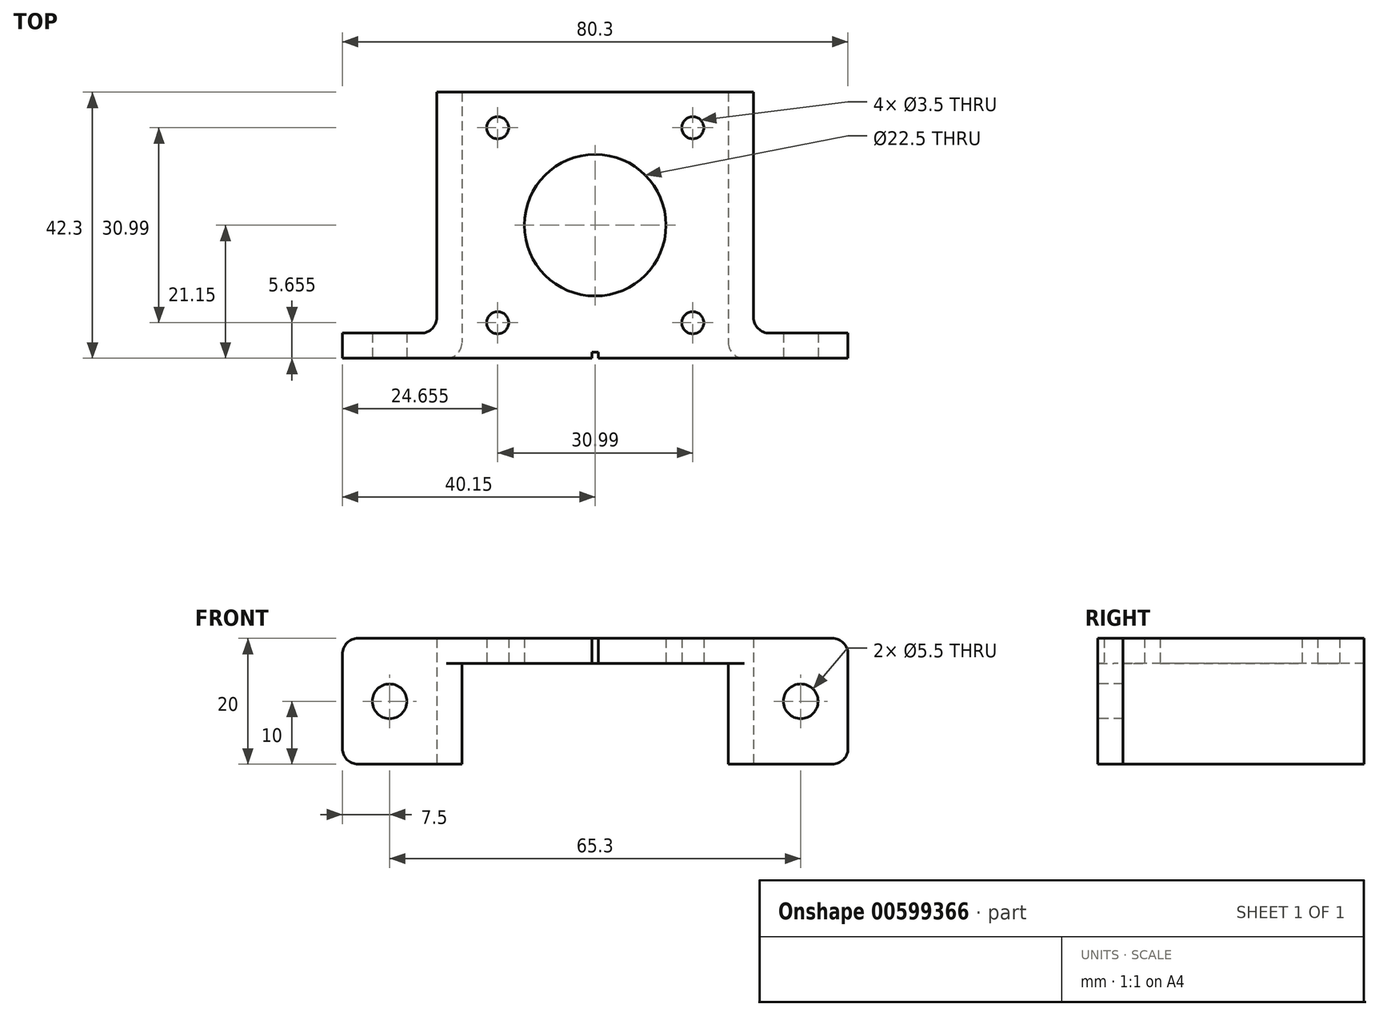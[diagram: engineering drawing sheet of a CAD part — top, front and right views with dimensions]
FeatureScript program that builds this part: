
annotation { "Feature Type Name" : "Feature", "Feature Type Description" : "" }
export const myFeature = defineFeature(function(context is Context, id is Id, definition is map)
    precondition{}
    {
        {
            var Q0;
            Q0=qCreatedBy(makeId("Top.planeOp"),FACE);
            var sketch = newSketch(context, id + "F0", { "sketchPlane" : qUnion([Q0])});
            skLineSegment(sketch, "E0.bottom", {"start": v(-21.15, 21.15) * mm, "end": v(21.15, 21.15) * mm});
            skLineSegment(sketch, "E0.left", {"start": v(-21.15, 21.15) * mm, "end": v(-21.15, -21.15) * mm, "construction": true});
            skLineSegment(sketch, "E0.right", {"start": v(21.15, 21.15) * mm, "end": v(21.15, -21.15) * mm, "construction": true});
            skLineSegment(sketch, "E1.bottom", {"start": v(-15.5, 15.5) * mm, "end": v(15.5, 15.5) * mm, "construction": true});
            skLineSegment(sketch, "E1.top", {"start": v(-15.5, -15.5) * mm, "end": v(15.5, -15.5) * mm, "construction": true});
            skLineSegment(sketch, "E1.left", {"start": v(-15.5, 15.5) * mm, "end": v(-15.5, -15.5) * mm, "construction": true});
            skLineSegment(sketch, "E1.right", {"start": v(15.5, 15.5) * mm, "end": v(15.5, -15.5) * mm, "construction": true});
            skCircle(sketch, "E2", {"center": v(-15.5, 15.5) * mm, "radius": 1.75 * mm});
            skCircle(sketch, "E3", {"center": v(-15.5, -15.5) * mm, "radius": 1.75 * mm});
            skCircle(sketch, "E4", {"center": v(15.5, 15.5) * mm, "radius": 1.75 * mm});
            skCircle(sketch, "E5", {"center": v(15.5, -15.5) * mm, "radius": 1.75 * mm});
            skCircle(sketch, "E6", {"center": v(0, 0) * mm, "radius": 11.25 * mm});
            skLineSegment(sketch, "E7", {"start": v(-21.15, -21.15) * mm, "end": v(21.15, -21.15) * mm});
            skLineSegment(sketch, "E8.bottom", {"start": v(21.15, -21.15) * mm, "end": v(40.15, -21.15) * mm});
            skLineSegment(sketch, "E8.top", {"start": v(21.15, -17.15) * mm, "end": v(40.15, -17.15) * mm});
            skLineSegment(sketch, "E8.left", {"start": v(21.15, -21.15) * mm, "end": v(21.15, -17.15) * mm});
            skLineSegment(sketch, "E8.right", {"start": v(40.15, -21.15) * mm, "end": v(40.15, -17.15) * mm});
            skLineSegment(sketch, "E9.bottom", {"start": v(-21.15, -21.15) * mm, "end": v(-40.15, -21.15) * mm});
            skLineSegment(sketch, "E9.top", {"start": v(-21.15, -17.15) * mm, "end": v(-40.15, -17.15) * mm});
            skLineSegment(sketch, "E9.left", {"start": v(-21.15, -21.15) * mm, "end": v(-21.15, -17.15) * mm});
            skLineSegment(sketch, "E9.right", {"start": v(-40.15, -21.15) * mm, "end": v(-40.15, -17.15) * mm});
            skLineSegment(sketch, "E10.bottom", {"start": v(-21.15, 21.15) * mm, "end": v(-25.15, 21.15) * mm});
            skLineSegment(sketch, "E10.top", {"start": v(-21.15, -17.15) * mm, "end": v(-25.15, -17.15) * mm});
            skLineSegment(sketch, "E10.left", {"start": v(-21.15, 21.15) * mm, "end": v(-21.15, -17.15) * mm});
            skLineSegment(sketch, "E10.right", {"start": v(-25.15, 21.15) * mm, "end": v(-25.15, -17.15) * mm});
            skLineSegment(sketch, "E11.bottom", {"start": v(21.15, 21.15) * mm, "end": v(25.15, 21.15) * mm});
            skLineSegment(sketch, "E11.top", {"start": v(21.15, -17.15) * mm, "end": v(25.15, -17.15) * mm});
            skLineSegment(sketch, "E11.left", {"start": v(21.15, 21.15) * mm, "end": v(21.15, -17.15) * mm});
            skLineSegment(sketch, "E11.right", {"start": v(25.15, 21.15) * mm, "end": v(25.15, -17.15) * mm});
            skSolve(sketch);
        }
        {
            var Q0;
            Q0=qSketchRegion(id+"F0",true);
            extrude(context, id + "F1", {"entities" : qUnion([Q0]), "depth" : 4 * mm});
        }
        {
            var Q0;
            Q0=makeQuery(id+"F1.opExtrude","CAP_FACE",FACE,{"disambiguationData":[OSD([sQuery(id+"F0.wireOp",EDGE,"E0.bottom"),sQuery(id+"F0.wireOp",EDGE,"E2"),sQuery(id+"F0.wireOp",EDGE,"E3"),sQuery(id+"F0.wireOp",EDGE,"E4"),sQuery(id+"F0.wireOp",EDGE,"E5"),sQuery(id+"F0.wireOp",EDGE,"E6"),sQuery(id+"F0.wireOp",EDGE,"E7"),sQuery(id+"F0.wireOp",EDGE,"E8.bottom"),sQuery(id+"F0.wireOp",EDGE,"E8.top"),sQuery(id+"F0.wireOp",EDGE,"E8.right"),sQuery(id+"F0.wireOp",EDGE,"E9.bottom"),sQuery(id+"F0.wireOp",EDGE,"E9.top"),sQuery(id+"F0.wireOp",EDGE,"E9.right"),sQuery(id+"F0.wireOp",EDGE,"E10.bottom"),sQuery(id+"F0.wireOp",EDGE,"E10.right"),sQuery(id+"F0.wireOp",EDGE,"E11.bottom"),sQuery(id+"F0.wireOp",EDGE,"E11.right")])],"isStart":true});
            var sketch = newSketch(context, id + "F2", { "sketchPlane" : qUnion([Q0])});
            skLineSegment(sketch, "E12.0", {"start": v(-21.15, -21.15) * mm, "end": v(-21.15, 17.15) * mm});
            skLineSegment(sketch, "E13.0", {"start": v(-21.15, 21.15) * mm, "end": v(-21.15, 17.15) * mm});
            skLineSegment(sketch, "E14.0", {"start": v(-21.15, 21.15) * mm, "end": v(-40.15, 21.15) * mm});
            skLineSegment(sketch, "E15.0", {"start": v(-40.15, 21.15) * mm, "end": v(-40.15, 17.15) * mm});
            skLineSegment(sketch, "E16.0", {"start": v(-25.15, -21.15) * mm, "end": v(-25.15, 17.15) * mm});
            skLineSegment(sketch, "E17.0", {"start": v(-25.15, 17.15) * mm, "end": v(-40.15, 17.15) * mm});
            skLineSegment(sketch, "E18.0", {"start": v(-21.15, -21.15) * mm, "end": v(-25.15, -21.15) * mm});
            skLineSegment(sketch, "E19.0", {"start": v(21.15, -21.15) * mm, "end": v(25.15, -21.15) * mm});
            skLineSegment(sketch, "E20.0", {"start": v(21.15, -21.15) * mm, "end": v(21.15, 17.15) * mm});
            skLineSegment(sketch, "E21.0", {"start": v(25.15, -21.15) * mm, "end": v(25.15, 17.15) * mm});
            skLineSegment(sketch, "E22.0", {"start": v(25.15, 17.15) * mm, "end": v(40.15, 17.15) * mm});
            skLineSegment(sketch, "E23.0", {"start": v(40.15, 21.15) * mm, "end": v(40.15, 17.15) * mm});
            skLineSegment(sketch, "E24.0", {"start": v(21.15, 21.15) * mm, "end": v(40.15, 21.15) * mm});
            skLineSegment(sketch, "E25.0", {"start": v(21.15, 21.15) * mm, "end": v(21.15, 17.15) * mm});
            skPoint(sketch, "E26.orphan", {"position": v(-21.15, 17.15) * mm});
            skPoint(sketch, "E27.orphan", {"position": v(21.15, 17.15) * mm});
            skSolve(sketch);
        }
        {
            var Q0;
            Q0=qSketchRegion(id+"F2",true);
            extrude(context, id + "F3", {"entities" : qUnion([Q0]), "operationType" : NewBodyOperationType.ADD, "depth" : 16 * mm});
        }
        {
            var Q0;
            Q0=makeQuery(id+"F3.boolean.opBoolean","MERGE",FACE,{"derivedFrom":[makeQuery(id+"F1.opExtrude","SWEPT_FACE",FACE,{"disambiguationData":[OSD([sQuery(id+"F0.wireOp",EDGE,"E7"),sQuery(id+"F0.wireOp",EDGE,"E8.bottom"),sQuery(id+"F0.wireOp",EDGE,"E9.bottom")])]}),makeQuery(id+"F3.opExtrude","SWEPT_FACE",FACE,{"disambiguationData":[OSD([sQuery(id+"F2.wireOp",EDGE,"E14.0")])]}),makeQuery(id+"F3.opExtrude","SWEPT_FACE",FACE,{"disambiguationData":[OSD([sQuery(id+"F2.wireOp",EDGE,"E24.0")])]})]});
            var sketch = newSketch(context, id + "F4", { "sketchPlane" : qUnion([Q0])});
            skCircle(sketch, "E28", {"center": v(-32.65, -6) * mm, "radius": 2.75 * mm});
            skCircle(sketch, "E29", {"center": v(32.65, -6) * mm, "radius": 2.75 * mm});
            skSolve(sketch);
        }
        {
            var Q0;
            Q0=qSketchRegion(id+"F4",true);
            extrude(context, id + "F5", {"entities" : qUnion([Q0]), "operationType" : NewBodyOperationType.REMOVE, "endBound" : BoundingType.UP_TO_NEXT, "oppositeDirection" : true, "depth" : 25 * mm});
        }
        {
            var Q0;
            Q0=makeQuery(id+"F1.opExtrude","CAP_EDGE",EDGE,{"disambiguationData":[OSD([sQuery(id+"F0.wireOp",EDGE,"E9.right")])],"isStart":false});
            var Q1;
            Q1=makeQuery(id+"F3.opExtrude","CAP_EDGE",EDGE,{"disambiguationData":[OSD([sQuery(id+"F2.wireOp",EDGE,"E15.0")])],"isStart":false});
            var Q2;
            Q2=makeQuery(id+"F3.opExtrude","CAP_EDGE",EDGE,{"disambiguationData":[OSD([sQuery(id+"F2.wireOp",EDGE,"E23.0")])],"isStart":false});
            var Q3;
            Q3=makeQuery(id+"F1.opExtrude","CAP_EDGE",EDGE,{"disambiguationData":[OSD([sQuery(id+"F0.wireOp",EDGE,"E8.right")])],"isStart":false});
            var Q4;
            Q4=makeQuery(id+"F3.boolean.opBoolean","MERGE",EDGE,{"derivedFrom":[makeQuery(id+"F1.opExtrude","SWEPT_EDGE",EDGE,{"disambiguationData":[OSD([sQuery(id+"F0.wireOp",EDGE,"E8.top"),sQuery(id+"F0.wireOp",EDGE,"E11.top"),sQuery(id+"F0.wireOp",EDGE,"E11.right")])]}),makeQuery(id+"F3.opExtrude","SWEPT_EDGE",EDGE,{"disambiguationData":[OSD([sQuery(id+"F2.wireOp",EDGE,"E21.0"),sQuery(id+"F2.wireOp",EDGE,"E22.0")])]})]});
            var Q5;
            Q5=makeQuery(id+"F3.boolean.opBoolean","MERGE",EDGE,{"derivedFrom":[makeQuery(id+"F1.opExtrude","SWEPT_EDGE",EDGE,{"disambiguationData":[OSD([sQuery(id+"F0.wireOp",EDGE,"E9.top"),sQuery(id+"F0.wireOp",EDGE,"E10.top"),sQuery(id+"F0.wireOp",EDGE,"E10.right")])]}),makeQuery(id+"F3.opExtrude","SWEPT_EDGE",EDGE,{"disambiguationData":[OSD([sQuery(id+"F2.wireOp",EDGE,"E16.0"),sQuery(id+"F2.wireOp",EDGE,"E17.0")])]})]});
            var Q6;
            Q6=makeQuery(id+"F3.opExtrude","SWEPT_EDGE",EDGE,{"disambiguationData":[OSD([sQuery(id+"F0.wireOp",EDGE,"E7"),sQuery(id+"F0.wireOp",EDGE,"E8.bottom"),sQuery(id+"F0.wireOp",EDGE,"E9.bottom"),sQuery(id+"F2.wireOp",EDGE,"E24.0"),sQuery(id+"F2.wireOp",EDGE,"E25.0")])]});
            var Q7;
            Q7=makeQuery(id+"F3.opExtrude","SWEPT_EDGE",EDGE,{"disambiguationData":[OSD([sQuery(id+"F0.wireOp",EDGE,"E7"),sQuery(id+"F0.wireOp",EDGE,"E8.bottom"),sQuery(id+"F0.wireOp",EDGE,"E9.bottom"),sQuery(id+"F2.wireOp",EDGE,"E13.0"),sQuery(id+"F2.wireOp",EDGE,"E14.0")])]});
            fillet(context, id + "F6", {"entities" : qUnion([Q0, Q1, Q2, Q3, Q4, Q5, Q6, Q7]), "radius" : 2.5 * mm, "tangentPropagation" : true, "allowEdgeOverflow" : false});
        }
        {
            var Q0;
            Q0=makeQuery(id+"F3.boolean.opBoolean","MERGE",FACE,{"derivedFrom":[makeQuery(id+"F1.opExtrude","SWEPT_FACE",FACE,{"disambiguationData":[OSD([sQuery(id+"F0.wireOp",EDGE,"E7"),sQuery(id+"F0.wireOp",EDGE,"E8.bottom"),sQuery(id+"F0.wireOp",EDGE,"E9.bottom")])]}),makeQuery(id+"F3.opExtrude","SWEPT_FACE",FACE,{"disambiguationData":[OSD([sQuery(id+"F2.wireOp",EDGE,"E14.0")])]}),makeQuery(id+"F3.opExtrude","SWEPT_FACE",FACE,{"disambiguationData":[OSD([sQuery(id+"F2.wireOp",EDGE,"E24.0")])]})]});
            var sketch = newSketch(context, id + "F7", { "sketchPlane" : qUnion([Q0])});
            skLineSegment(sketch, "E30.bottom", {"start": v(0, 4) * mm, "end": v(0.5, 4) * mm});
            skLineSegment(sketch, "E30.top", {"start": v(0, 0) * mm, "end": v(0.5, 0) * mm});
            skLineSegment(sketch, "E30.left", {"start": v(0, 4) * mm, "end": v(0, 0) * mm});
            skLineSegment(sketch, "E30.right", {"start": v(0.5, 4) * mm, "end": v(0.5, 0) * mm});
            skLineSegment(sketch, "E31.MirrorCS", {"start": v(-0.5, 4) * mm, "end": v(-0.5, 0) * mm});
            skLineSegment(sketch, "E32.MirrorCS", {"start": v(0, 0) * mm, "end": v(-0.5, 0) * mm});
            skLineSegment(sketch, "E33.MirrorCS", {"start": v(0, 4) * mm, "end": v(-0.5, 4) * mm});
            skSolve(sketch);
        }
        {
            var Q0;
            Q0=qSketchRegion(id+"F7",true);
            extrude(context, id + "F8", {"entities" : qUnion([Q0]), "operationType" : NewBodyOperationType.REMOVE, "oppositeDirection" : true, "depth" : 1 * mm});
        }
    });
